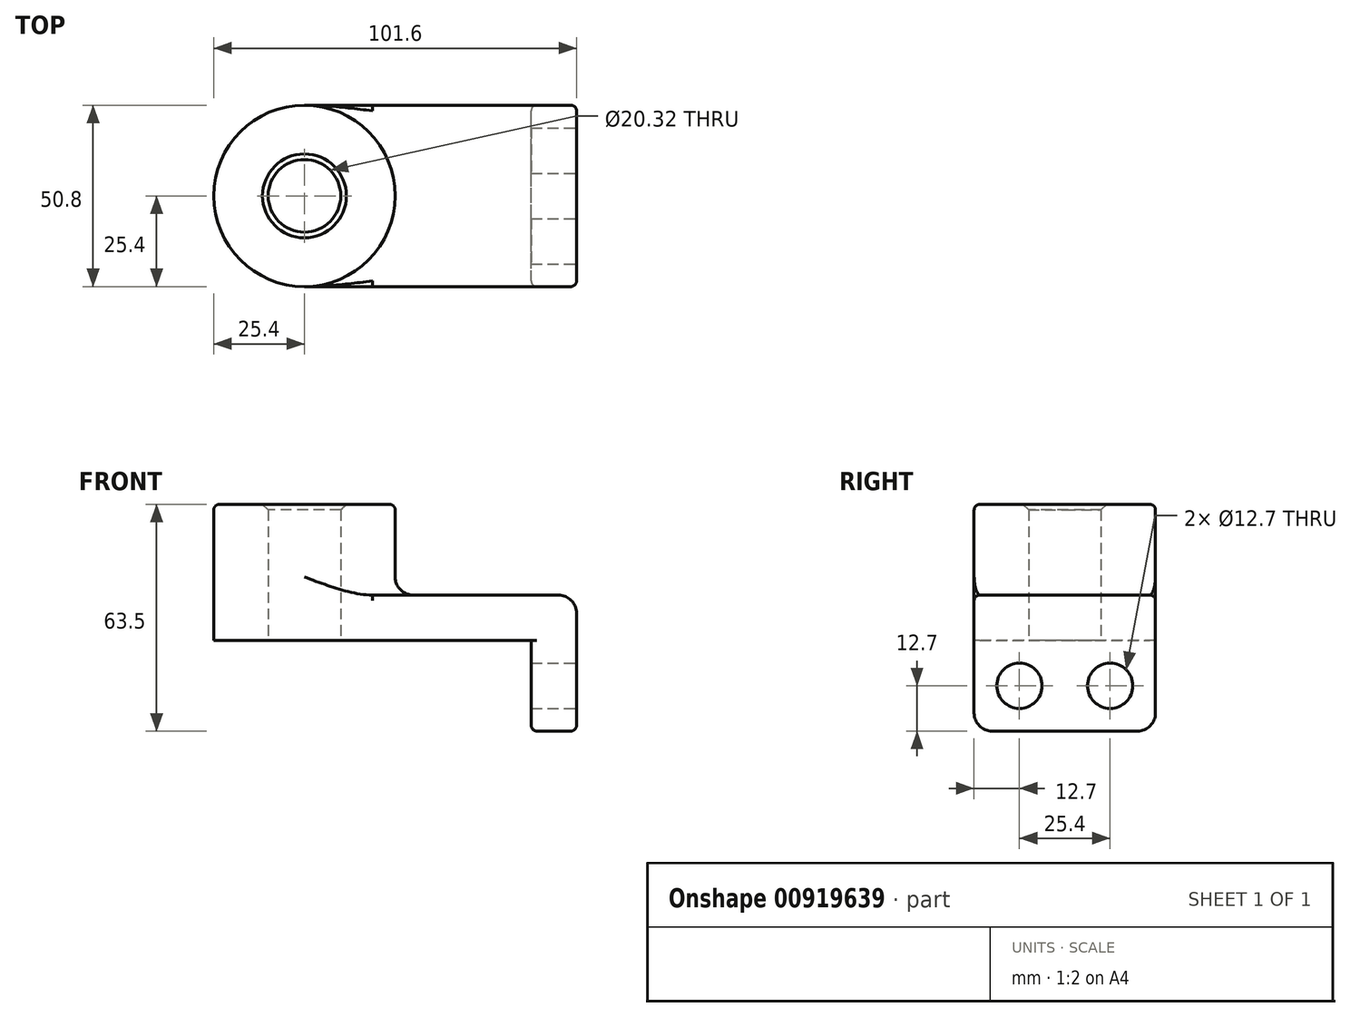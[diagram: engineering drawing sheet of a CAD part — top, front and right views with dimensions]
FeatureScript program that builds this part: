
annotation { "Feature Type Name" : "Feature", "Feature Type Description" : "" }
export const myFeature = defineFeature(function(context is Context, id is Id, definition is map)
    precondition{}
    {
        {
            var Q0;
            Q0=qCreatedBy(makeId("Top.planeOp"),FACE);
            var sketch = newSketch(context, id + "F0", { "sketchPlane" : qUnion([Q0])});
            skLineSegment(sketch, "E0.bottom", {"start": v(38.1, -25.4) * mm, "end": v(-38.1, -25.4) * mm});
            skLineSegment(sketch, "E0.top", {"start": v(38.1, 25.4) * mm, "end": v(-38.1, 25.4) * mm});
            skLineSegment(sketch, "E0.left", {"start": v(38.1, -25.4) * mm, "end": v(38.1, 25.4) * mm});
            skLineSegment(sketch, "E0.right", {"start": v(-38.1, -25.4) * mm, "end": v(-38.1, 25.4) * mm});
            skPoint(sketch, "E0.middle", {"position": v(0, 0) * mm});
            skCircle(sketch, "E1", {"center": v(-38.1, 0) * mm, "radius": 25.4 * mm});
            skCircle(sketch, "E2", {"center": v(-38.1, 0) * mm, "radius": 10.16 * mm});
            skSolve(sketch);
        }
        {
            var Q0;
            {var subQ0=sQuery(id+"F0.wireOp",EDGE,"E0.bottom");Q0=makeQuery(id+"F0.imprint","IMPRINT",FACE,{"disambiguationData":[TD([[makeQuery(id+"F0.imprint","IMPRINT",EDGE,{"derivedFrom":subQ0}),-1.0]])]});}
            var Q1;
            {var subQ0=sQuery(id+"F0.wireOp",EDGE,"E0.bottom");Q1=makeQuery(id+"F0.imprint","IMPRINT",FACE,{"disambiguationData":[TD([[makeQuery(id+"F0.imprint","IMPRINT",EDGE,{"derivedFrom":subQ0}),-1.0]])]});}
            var Q2;
            {var subQ1=sQuery(id+"F0.wireOp",EDGE,"E0.right");var subQ3=sQuery(id+"F0.wireOp",EDGE,"E2");var subQ4=makeQuery(id+"F0.imprint","INTERSECT",VERTEX,{"disambiguationData":[OD(0.0)],"derivedFrom":[subQ1,subQ3]});Q2=makeQuery(id+"F0.imprint","IMPRINT",FACE,{"disambiguationData":[TD([[makeQuery(id+"F0.imprint","IMPRINT",EDGE,{"disambiguationData":[TD([[subQ4,1.0]])],"derivedFrom":subQ3}),-1.0]])]});}
            var Q3;
            {var subQ1=sQuery(id+"F0.wireOp",EDGE,"E0.right");var subQ3=sQuery(id+"F0.wireOp",EDGE,"E2");var subQ4=makeQuery(id+"F0.imprint","INTERSECT",VERTEX,{"disambiguationData":[OD(0.0)],"derivedFrom":[subQ1,subQ3]});Q3=makeQuery(id+"F0.imprint","IMPRINT",FACE,{"disambiguationData":[TD([[makeQuery(id+"F0.imprint","IMPRINT",EDGE,{"disambiguationData":[TD([[subQ4,-1.0]])],"derivedFrom":subQ3}),-1.0]])]});}
            extrude(context, id + "F1", {"entities" : qUnion([Q0, Q1, Q2, Q3]), "depth" : 12.7 * mm, "offsetDistance" : 25.4 * mm});
        }
        {
            var Q0;
            {var subQ1=sQuery(id+"F0.wireOp",EDGE,"E0.right");var subQ3=sQuery(id+"F0.wireOp",EDGE,"E2");var subQ4=makeQuery(id+"F0.imprint","INTERSECT",VERTEX,{"disambiguationData":[OD(0.0)],"derivedFrom":[subQ1,subQ3]});Q0=makeQuery(id+"F0.imprint","IMPRINT",FACE,{"disambiguationData":[TD([[makeQuery(id+"F0.imprint","IMPRINT",EDGE,{"disambiguationData":[TD([[subQ4,1.0]])],"derivedFrom":subQ3}),-1.0]])]});}
            var Q1;
            {var subQ1=sQuery(id+"F0.wireOp",EDGE,"E0.right");var subQ3=sQuery(id+"F0.wireOp",EDGE,"E2");var subQ4=makeQuery(id+"F0.imprint","INTERSECT",VERTEX,{"disambiguationData":[OD(0.0)],"derivedFrom":[subQ1,subQ3]});Q1=makeQuery(id+"F0.imprint","IMPRINT",FACE,{"disambiguationData":[TD([[makeQuery(id+"F0.imprint","IMPRINT",EDGE,{"disambiguationData":[TD([[subQ4,-1.0]])],"derivedFrom":subQ3}),-1.0]])]});}
            var Q2;
            {var subQ1=sQuery(id+"F0.wireOp",EDGE,"E0.right");var subQ3=sQuery(id+"F0.wireOp",EDGE,"E2");var subQ4=makeQuery(id+"F0.imprint","INTERSECT",VERTEX,{"disambiguationData":[OD(0.0)],"derivedFrom":[subQ1,subQ3]});Q2=makeQuery(id+"F0.imprint","IMPRINT",FACE,{"disambiguationData":[TD([[makeQuery(id+"F0.imprint","IMPRINT",EDGE,{"disambiguationData":[TD([[subQ4,-1.0]])],"derivedFrom":subQ3}),-1.0]])]});}
            var Q3;
            {var subQ1=sQuery(id+"F0.wireOp",EDGE,"E0.right");var subQ3=sQuery(id+"F0.wireOp",EDGE,"E2");var subQ4=makeQuery(id+"F0.imprint","INTERSECT",VERTEX,{"disambiguationData":[OD(0.0)],"derivedFrom":[subQ1,subQ3]});Q3=makeQuery(id+"F0.imprint","IMPRINT",FACE,{"disambiguationData":[TD([[makeQuery(id+"F0.imprint","IMPRINT",EDGE,{"disambiguationData":[TD([[subQ4,1.0]])],"derivedFrom":subQ3}),-1.0]])]});}
            extrude(context, id + "F2", {"entities" : qUnion([Q0, Q1, Q2, Q3]), "operationType" : NewBodyOperationType.ADD, "depth" : 38.1 * mm, "offsetDistance" : 25.4 * mm});
        }
        {
            var Q0;
            Q0=makeQuery(id+"F1.opExtrude","SWEPT_FACE",FACE,{"disambiguationData":[OSD([sQuery(id+"F0.wireOp",EDGE,"E0.left")])]});
            var sketch = newSketch(context, id + "F3", { "sketchPlane" : qUnion([Q0])});
            skLineSegment(sketch, "E3.bottom", {"start": v(-25.4, 12.7) * mm, "end": v(25.4, 12.7) * mm});
            skLineSegment(sketch, "E3.top", {"start": v(-25.4, -25.4) * mm, "end": v(25.4, -25.4) * mm});
            skLineSegment(sketch, "E3.left", {"start": v(-25.4, 12.7) * mm, "end": v(-25.4, -25.4) * mm});
            skLineSegment(sketch, "E3.right", {"start": v(25.4, 12.7) * mm, "end": v(25.4, -25.4) * mm});
            skLineSegment(sketch, "E4", {"start": v(0, 0) * mm, "end": v(0, -25.4) * mm});
            skCircle(sketch, "E5", {"center": v(-12.7, -12.7) * mm, "radius": 6.35 * mm});
            skCircle(sketch, "E6.MirrorC", {"center": v(12.7, -12.7) * mm, "radius": 6.35 * mm});
            skSolve(sketch);
        }
        {
            var Q0;
            {var subQ0=sQuery(id+"F3.wireOp",EDGE,"E4");Q0=makeQuery(id+"F3.imprint","IMPRINT",FACE,{"disambiguationData":[TD([[makeQuery(id+"F3.imprint","IMPRINT",EDGE,{"derivedFrom":subQ0}),-1.0]])]});}
            var Q1;
            {var subQ5=sQuery(id+"F3.wireOp",EDGE,"E4");Q1=makeQuery(id+"F3.imprint","IMPRINT",FACE,{"disambiguationData":[TD([[makeQuery(id+"F3.imprint","IMPRINT",EDGE,{"derivedFrom":subQ5}),1.0]])]});}
            extrude(context, id + "F4", {"entities" : qUnion([Q0, Q1]), "operationType" : NewBodyOperationType.ADD, "oppositeDirection" : true, "depth" : 12.7 * mm, "offsetDistance" : 25.4 * mm});
        }
        {
            var Q0;
            {var subQ0=sQuery(id+"F0.wireOp",EDGE,"E1");Q0=makeQuery(id+"F2.boolean.opBoolean","INTERSECT",EDGE,{"derivedFrom":[makeQuery(id+"F1.opExtrude","CAP_FACE",FACE,{"disambiguationData":[OSD([sQuery(id+"F0.wireOp",EDGE,"E0.bottom"),sQuery(id+"F0.wireOp",EDGE,"E0.top"),sQuery(id+"F0.wireOp",EDGE,"E0.left"),subQ0,sQuery(id+"F0.wireOp",EDGE,"E2")])],"isStart":false}),makeQuery(id+"F2.opExtrude","SWEPT_FACE",FACE,{"disambiguationData":[OSD([subQ0])]})]});}
            var Q1;
            Q1=makeQuery(id+"F4.opExtrude","SWEPT_EDGE",EDGE,{"disambiguationData":[OSD([sQuery(id+"F3.wireOp",EDGE,"E3.top"),sQuery(id+"F3.wireOp",EDGE,"E3.left")])]});
            var Q2;
            Q2=makeQuery(id+"F4.opExtrude","SWEPT_EDGE",EDGE,{"disambiguationData":[OSD([sQuery(id+"F3.wireOp",EDGE,"E3.top"),sQuery(id+"F3.wireOp",EDGE,"E3.right")])]});
            var Q3;
            Q3=makeQuery(id+"F1.opExtrude","CAP_EDGE",EDGE,{"disambiguationData":[OSD([sQuery(id+"F0.wireOp",EDGE,"E0.left")])],"isStart":false});
            var Q4;
            Q4=makeQuery(id+"F4.opExtrude","CAP_EDGE",EDGE,{"disambiguationData":[OSD([sQuery(id+"F0.wireOp",EDGE,"E0.left")])],"isStart":false});
            fillet(context, id + "F5", {"entities" : qUnion([Q0, Q1, Q2, Q3, Q4]), "radius" : 5.08 * mm, "tangentPropagation" : true, "allowEdgeOverflow" : false});
        }
        {
            var Q0;
            Q0=makeQuery(id+"F2.opExtrude","CAP_EDGE",EDGE,{"disambiguationData":[OSD([sQuery(id+"F0.wireOp",EDGE,"E1")])],"isStart":false});
            var Q1;
            Q1=makeQuery(id+"F1.opExtrude","CAP_EDGE",EDGE,{"disambiguationData":[OSD([sQuery(id+"F0.wireOp",EDGE,"E0.bottom")])],"isStart":false});
            var Q2;
            Q2=makeQuery(id+"F4.opExtrude","CAP_EDGE",EDGE,{"disambiguationData":[OSD([sQuery(id+"F3.wireOp",EDGE,"E3.left")])],"isStart":false});
            fillet(context, id + "F6", {"entities" : qUnion([Q0, Q1, Q2]), "radius" : 1.59 * mm, "tangentPropagation" : true, "allowEdgeOverflow" : false});
        }
        {
            var Q0;
            Q0=makeQuery(id+"F2.opExtrude","CAP_EDGE",EDGE,{"disambiguationData":[OSD([sQuery(id+"F0.wireOp",EDGE,"E2")])],"isStart":false});
            chamfer(context, id + "F7", {"entities" : qUnion([Q0]), "width" : 1.59 * mm, "tangentPropagation" : true});
        }
    });
